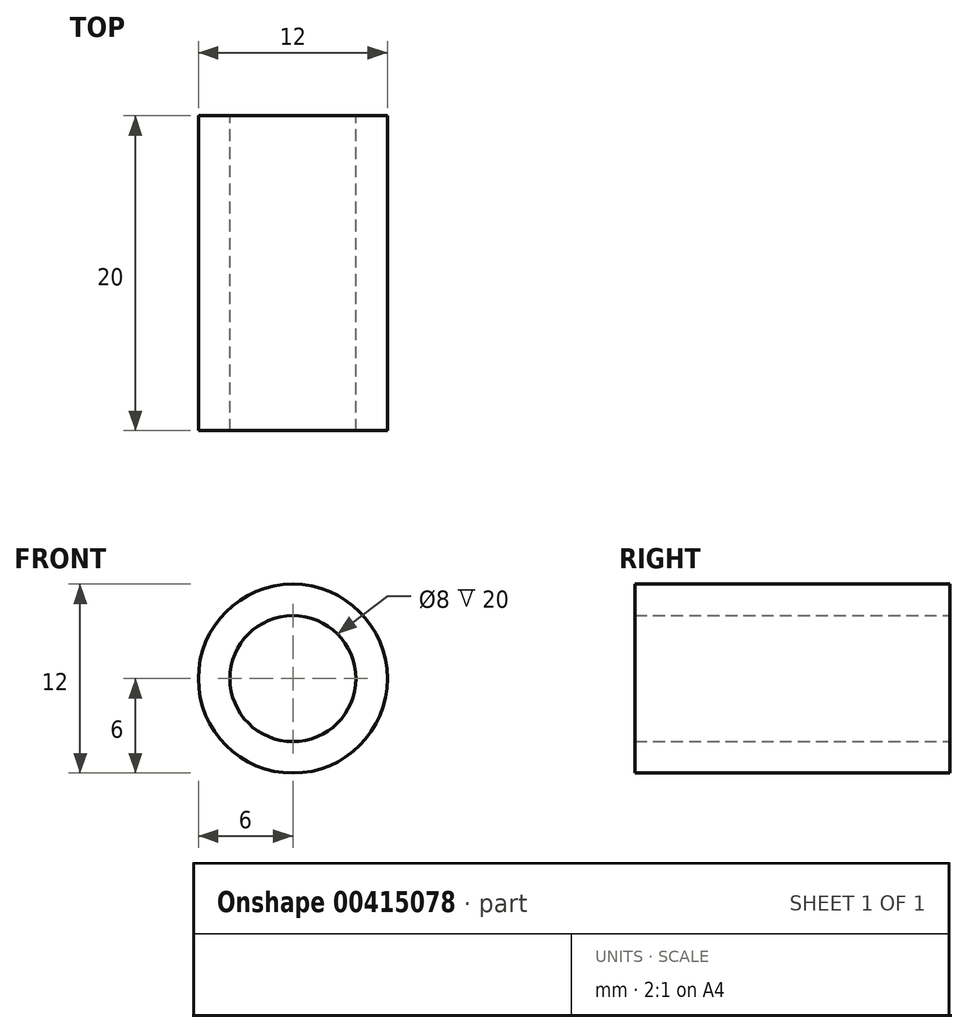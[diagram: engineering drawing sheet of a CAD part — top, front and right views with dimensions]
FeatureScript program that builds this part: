
annotation { "Feature Type Name" : "Feature", "Feature Type Description" : "" }
export const myFeature = defineFeature(function(context is Context, id is Id, definition is map)
    precondition{}
    {
        {
            var Q0;
            Q0=qCreatedBy(makeId("Front.planeOp"),FACE);
            var sketch = newSketch(context, id + "F0", { "sketchPlane" : qUnion([Q0])});
            skCircle(sketch, "E0", {"center": v(0, 0) * mm, "radius": 4 * mm});
            skCircle(sketch, "E1", {"center": v(0, 0) * mm, "radius": 6 * mm});
            skSolve(sketch);
        }
        {
            var Q0;
            Q0 = qSketchRegion(id + "F0", true);
            extrude(context, id + "F1", {"entities" : qUnion([Q0]), "depth" : 20 * mm});
        }
    });
